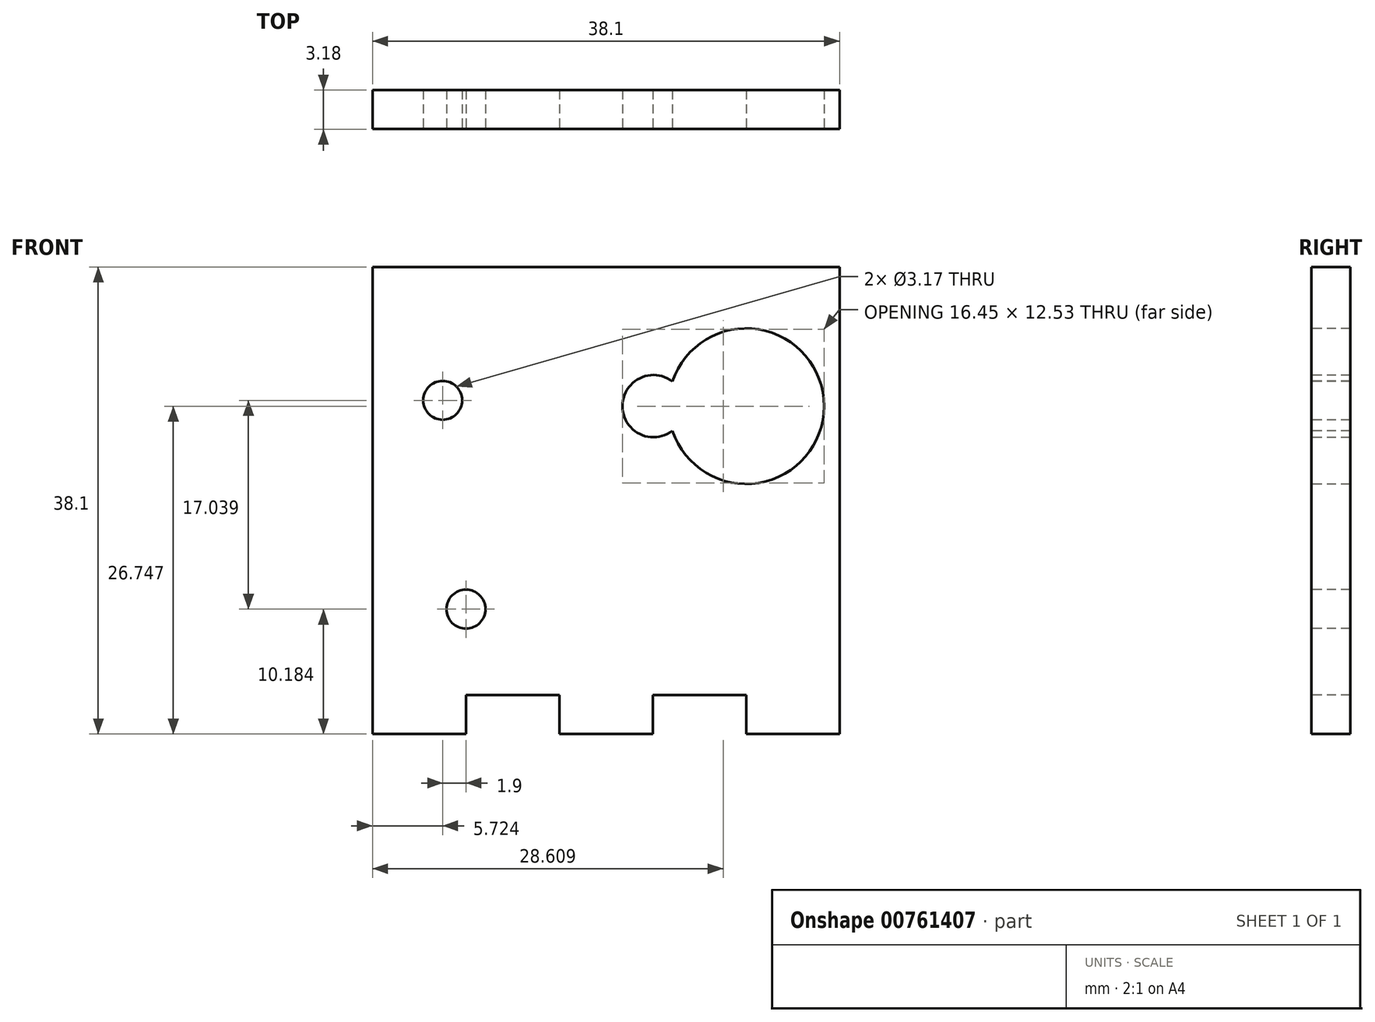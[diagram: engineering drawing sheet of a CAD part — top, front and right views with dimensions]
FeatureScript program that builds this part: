
annotation { "Feature Type Name" : "Feature", "Feature Type Description" : "" }
export const myFeature = defineFeature(function(context is Context, id is Id, definition is map)
    precondition{}
    {
        {
            var Q0;
            Q0=qCreatedBy(makeId("Front.planeOp"),FACE);
            var sketch = newSketch(context, id + "F0", { "sketchPlane" : qUnion([Q0])});
            skPoint(sketch, "E0.middle", {"position": v(0, 0) * mm});
            skLineSegment(sketch, "E1.bottom", {"start": v(-25.26, 16.76) * mm, "end": v(12.84, 16.76) * mm});
            skLineSegment(sketch, "E1.top", {"start": v(-25.26, -21.34) * mm, "end": v(12.84, -21.34) * mm});
            skLineSegment(sketch, "E1.left", {"start": v(-25.26, 16.76) * mm, "end": v(-25.26, -21.34) * mm});
            skLineSegment(sketch, "E1.right", {"start": v(12.84, 16.76) * mm, "end": v(12.84, -21.34) * mm});
            skSolve(sketch);
        }
        {
            var Q0;
            Q0 = qSketchRegion(id + "F0", true);
            extrude(context, id + "F1", {"entities" : qUnion([Q0]), "depth" : 3.17 * mm, "offsetDistance" : 25.4 * mm});
        }
        {
            var Q0;
            Q0=makeQuery(id+"F1.opExtrude","CAP_FACE",FACE,{"disambiguationData":[OSD([sQuery(id+"F0.wireOp",EDGE,"E1.bottom"),sQuery(id+"F0.wireOp",EDGE,"E1.top"),sQuery(id+"F0.wireOp",EDGE,"E1.left"),sQuery(id+"F0.wireOp",EDGE,"E1.right")])],"isStart":false});
            var sketch = newSketch(context, id + "F2", { "sketchPlane" : qUnion([Q0])});
            skLineSegment(sketch, "E2.bottom", {"start": v(-25.26, 16.76) * mm, "end": v(12.84, 16.76) * mm});
            skLineSegment(sketch, "E2.top", {"start": v(-25.26, -21.34) * mm, "end": v(-17.64, -21.34) * mm});
            skLineSegment(sketch, "E2.left", {"start": v(-25.26, 19.3) * mm, "end": v(-25.26, -21.34) * mm});
            skLineSegment(sketch, "E2.right", {"start": v(12.84, 16.76) * mm, "end": v(12.84, -21.34) * mm});
            skArc(sketch, "E3", {"start": v(-0.8, 3.39) * mm, "mid": v(11.57, 5.4) * mm, "end": v(-0.8, 7.43) * mm});
            skArc(sketch, "E4", {"start": v(-0.8, 7.43) * mm, "mid": v(-4.88, 5.4) * mm, "end": v(-0.8, 3.39) * mm});
            skCircle(sketch, "E5", {"center": v(-19.54, 5.88) * mm, "radius": 1.59 * mm});
            skCircle(sketch, "E6", {"center": v(-17.64, -11.16) * mm, "radius": 1.59 * mm});
            skLineSegment(sketch, "E7.bottom", {"start": v(-25.26, -18.16) * mm, "end": v(-17.64, -18.16) * mm});
            skLineSegment(sketch, "E7.left", {"start": v(-25.26, -18.16) * mm, "end": v(-25.26, -21.34) * mm});
            skLineSegment(sketch, "E7.right", {"start": v(-17.64, -18.16) * mm, "end": v(-17.64, -21.34) * mm});
            skLineSegment(sketch, "E8.bottom", {"start": v(-10.02, -18.16) * mm, "end": v(-2.4, -18.16) * mm});
            skLineSegment(sketch, "E8.top", {"start": v(-10.02, -21.34) * mm, "end": v(-2.4, -21.34) * mm});
            skLineSegment(sketch, "E8.left", {"start": v(-10.02, -18.16) * mm, "end": v(-10.02, -21.34) * mm});
            skLineSegment(sketch, "E8.right", {"start": v(-2.4, -18.16) * mm, "end": v(-2.4, -21.34) * mm});
            skLineSegment(sketch, "E9.bottom", {"start": v(5.22, -18.16) * mm, "end": v(12.84, -18.16) * mm});
            skLineSegment(sketch, "E9.top", {"start": v(5.22, -21.34) * mm, "end": v(12.84, -21.34) * mm});
            skLineSegment(sketch, "E9.left", {"start": v(5.22, -18.16) * mm, "end": v(5.22, -21.34) * mm});
            skLineSegment(sketch, "E9.right", {"start": v(12.84, -18.16) * mm, "end": v(12.84, -21.34) * mm});
            skLineSegment(sketch, "E10", {"start": v(-17.64, -18.16) * mm, "end": v(-10.02, -18.16) * mm});
            skLineSegment(sketch, "E11", {"start": v(-2.4, -18.16) * mm, "end": v(5.22, -18.16) * mm});
            skSolve(sketch);
        }
        {
            var Q0;
            Q0=makeQuery(id+"F2.imprint","IMPRINT",FACE,{"disambiguationData":[TD([[makeQuery(id+"F2.imprint","IMPRINT",EDGE,{"derivedFrom":sQuery(id+"F2.wireOp",EDGE,"E3")}),1.0]])]});
            var Q1;
            {var subQ0=sQuery(id+"F2.wireOp",EDGE,"E7.right");Q1=makeQuery(id+"F2.imprint","IMPRINT",FACE,{"disambiguationData":[TD([[makeQuery(id+"F2.imprint","IMPRINT",EDGE,{"derivedFrom":subQ0}),1.0]])]});}
            var Q2;
            {var subQ2=sQuery(id+"F2.wireOp",EDGE,"E8.right");Q2=makeQuery(id+"F2.imprint","IMPRINT",FACE,{"disambiguationData":[TD([[makeQuery(id+"F2.imprint","IMPRINT",EDGE,{"derivedFrom":subQ2}),1.0]])]});}
            var Q3;
            Q3=makeQuery(id+"F2.imprint","IMPRINT",FACE,{"disambiguationData":[TD([[makeQuery(id+"F2.imprint","IMPRINT",EDGE,{"derivedFrom":sQuery(id+"F2.wireOp",EDGE,"E5")}),1.0]])]});
            var Q4;
            Q4=makeQuery(id+"F2.imprint","IMPRINT",FACE,{"disambiguationData":[TD([[makeQuery(id+"F2.imprint","IMPRINT",EDGE,{"derivedFrom":sQuery(id+"F2.wireOp",EDGE,"E6")}),1.0]])]});
            extrude(context, id + "F3", {"entities" : qUnion([Q0, Q1, Q2, Q3, Q4]), "operationType" : NewBodyOperationType.REMOVE, "oppositeDirection" : true, "depth" : 3.17 * mm, "offsetDistance" : 25.4 * mm});
        }
    });
